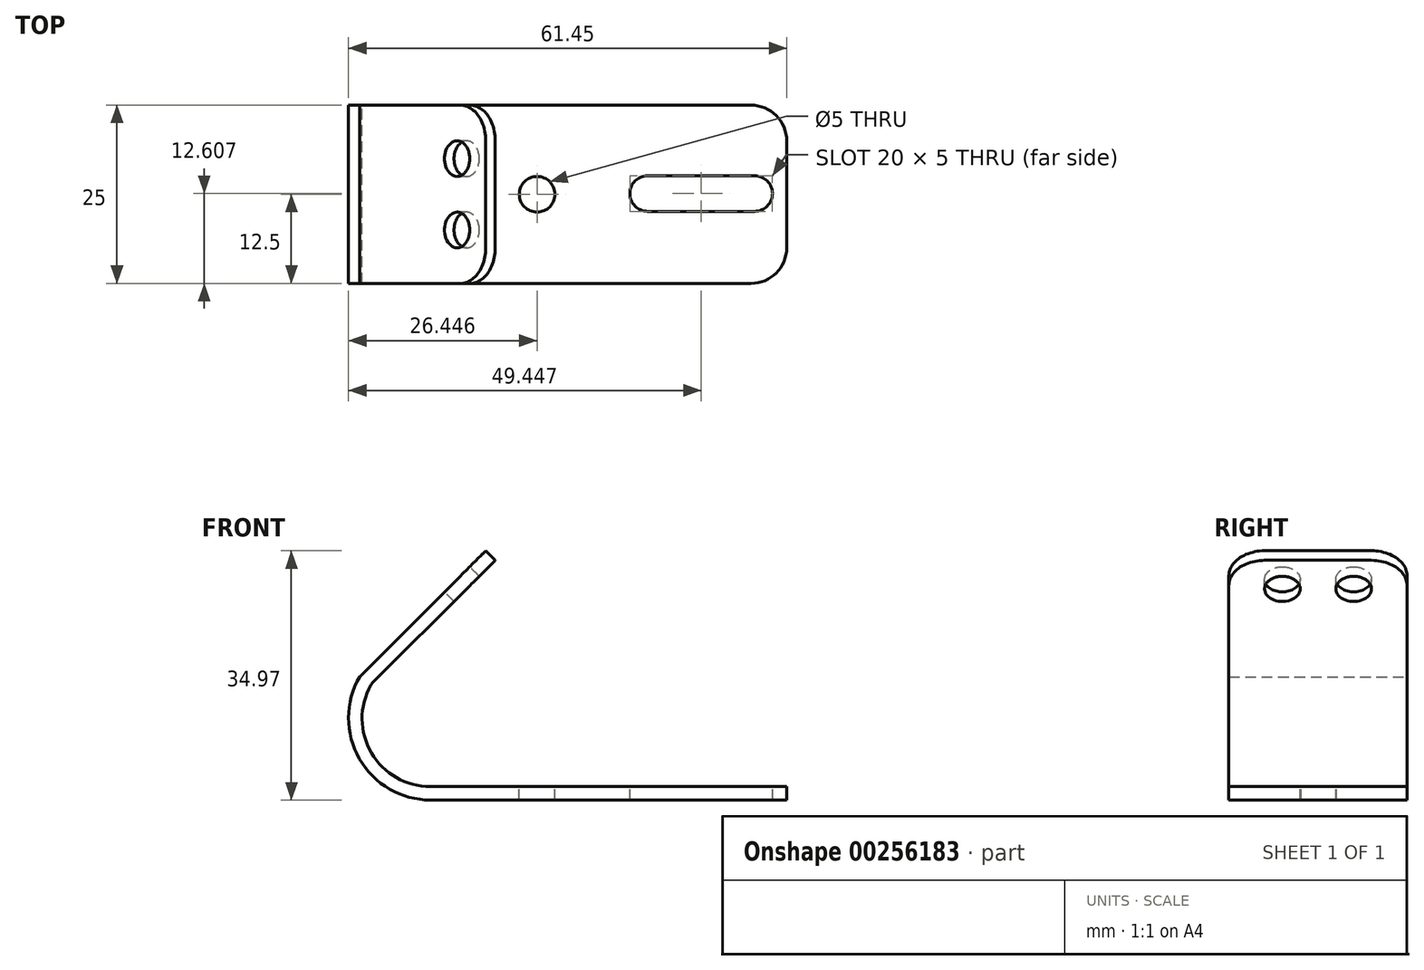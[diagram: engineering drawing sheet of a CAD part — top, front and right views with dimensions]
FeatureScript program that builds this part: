
annotation { "Feature Type Name" : "Feature", "Feature Type Description" : "" }
export const myFeature = defineFeature(function(context is Context, id is Id, definition is map)
    precondition{}
    {
        {
            var Q0;
            Q0=qCreatedBy(makeId("Front.planeOp"),FACE);
            var sketch = newSketch(context, id + "F0", { "sketchPlane" : qUnion([Q0])});
            skLineSegment(sketch, "E0", {"start": v(39.72, 0) * mm, "end": v(-10.22, 0) * mm});
            skLineSegment(sketch, "E1", {"start": v(39.72, 0) * mm, "end": v(39.72, 1.9) * mm});
            skLineSegment(sketch, "E2", {"start": v(39.72, 1.9) * mm, "end": v(-10.28, 1.9) * mm});
            skLineSegment(sketch, "E3", {"start": v(-18.53, 16.25) * mm, "end": v(-1.15, 33.63) * mm});
            skLineSegment(sketch, "E4", {"start": v(-1.15, 33.63) * mm, "end": v(-2.5, 34.97) * mm});
            skLineSegment(sketch, "E5", {"start": v(-2.5, 34.97) * mm, "end": v(-20.17, 17.3) * mm});
            skArc(sketch, "E6", {"start": v(-10.22, 0) * mm, "mid": v(-20.2, 5.77) * mm, "end": v(-20.17, 17.3) * mm});
            skArc(sketch, "E7", {"start": v(-10.28, 1.9) * mm, "mid": v(-18.56, 6.69) * mm, "end": v(-18.53, 16.25) * mm});
            skSolve(sketch);
        }
        {
            var Q0;
            Q0=makeQuery(id+"F0.imprint","IMPRINT",FACE,{"disambiguationData":[TD([[makeQuery(id+"F0.imprint","IMPRINT",EDGE,{"derivedFrom":sQuery(id+"F0.wireOp",EDGE,"E0")}),-1.0]])]});
            extrude(context, id + "F1", {"entities" : qUnion([Q0]), "endBound" : BoundingType.SYMMETRIC, "depth" : 25 * mm});
        }
        {
            var Q0;
            Q0=makeQuery(id+"F1.opExtrude","SWEPT_FACE",FACE,{"disambiguationData":[OSD([sQuery(id+"F0.wireOp",EDGE,"E2")])]});
            var sketch = newSketch(context, id + "F2", { "sketchPlane" : qUnion([Q0])});
            skPoint(sketch, "E8", {"position": v(0, 0) * mm});
            skCircle(sketch, "E9", {"center": v(4.72, 0) * mm, "radius": 2.5 * mm});
            skLineSegment(sketch, "E10", {"start": v(20.22, 2.6) * mm, "end": v(35.22, 2.6) * mm});
            skLineSegment(sketch, "E11", {"start": v(35.22, -2.4) * mm, "end": v(20.22, -2.4) * mm});
            skArc(sketch, "E12", {"start": v(35.22, 2.6) * mm, "mid": v(37.72, 0.1) * mm, "end": v(35.22, -2.4) * mm});
            skArc(sketch, "E13", {"start": v(20.22, -2.4) * mm, "mid": v(17.72, 0.1) * mm, "end": v(20.22, 2.6) * mm});
            skSolve(sketch);
        }
        {
            var Q0;
            Q0=makeQuery(id+"F2.imprint","IMPRINT",FACE,{"disambiguationData":[TD([[makeQuery(id+"F2.imprint","IMPRINT",EDGE,{"derivedFrom":sQuery(id+"F2.wireOp",EDGE,"E9")}),1.0]])]});
            var Q1;
            Q1=makeQuery(id+"F2.imprint","IMPRINT",FACE,{"disambiguationData":[TD([[makeQuery(id+"F2.imprint","IMPRINT",EDGE,{"derivedFrom":sQuery(id+"F2.wireOp",EDGE,"E10")}),-1.0]])]});
            extrude(context, id + "F3", {"entities" : qUnion([Q0, Q1]), "operationType" : NewBodyOperationType.REMOVE, "oppositeDirection" : true, "depth" : 25 * mm});
        }
        {
            var Q0;
            Q0=makeQuery(id+"F1.opExtrude","SWEPT_FACE",FACE,{"disambiguationData":[OSD([sQuery(id+"F0.wireOp",EDGE,"E5")])]});
            var sketch = newSketch(context, id + "F4", { "sketchPlane" : qUnion([Q0])});
            skPoint(sketch, "E14", {"position": v(-5, 17.3) * mm});
            skPoint(sketch, "E15", {"position": v(5, 17.3) * mm});
            skSolve(sketch);
        }
        {
            var Q0;
            Q0=sQuery(id+"F4.wireOp",VERTEX,"E14");
            var Q1;
            Q1=sQuery(id+"F4.wireOp",VERTEX,"E15");
            var Q2;
            Q2=makeQuery(id+"F1.opExtrude","SWEPT_BODY",BODY,{"disambiguationData":[OSD([sQuery(id+"F0.wireOp",EDGE,"E0"),sQuery(id+"F0.wireOp",EDGE,"E1"),sQuery(id+"F0.wireOp",EDGE,"E2"),sQuery(id+"F0.wireOp",EDGE,"E3"),sQuery(id+"F0.wireOp",EDGE,"E4"),sQuery(id+"F0.wireOp",EDGE,"E5"),sQuery(id+"F0.wireOp",EDGE,"E6"),sQuery(id+"F0.wireOp",EDGE,"E7")])]});
            hole(context, id + "F5", {"style" : HoleStyle.C_BORE, "endStyle" : HoleEndStyle.BLIND, "holeDiameter" : 5 * mm, "cBoreDiameter" : 5 * mm, "cBoreDepth" : 5 * mm, "holeDepth" : 12 * mm, "tappedDepth" : 12 * mm, "tapClearance" : 3, "locations" : qUnion([Q0, Q1]), "scope" : qUnion([Q2])});
        }
        {
            var Q0;
            Q0=makeQuery(id+"F1.opExtrude","CAP_EDGE",EDGE,{"disambiguationData":[OSD([sQuery(id+"F0.wireOp",EDGE,"E1")])],"isStart":false});
            var Q1;
            Q1=makeQuery(id+"F1.opExtrude","CAP_EDGE",EDGE,{"disambiguationData":[OSD([sQuery(id+"F0.wireOp",EDGE,"E1")])],"isStart":true});
            fillet(context, id + "F6", {"entities" : qUnion([Q0, Q1]), "radius" : 5 * mm, "tangentPropagation" : true, "allowEdgeOverflow" : false});
        }
        {
            var Q0;
            Q0=makeQuery(id+"F1.opExtrude","CAP_EDGE",EDGE,{"disambiguationData":[OSD([sQuery(id+"F0.wireOp",EDGE,"E4")])],"isStart":false});
            var Q1;
            Q1=makeQuery(id+"F1.opExtrude","CAP_EDGE",EDGE,{"disambiguationData":[OSD([sQuery(id+"F0.wireOp",EDGE,"E4")])],"isStart":true});
            fillet(context, id + "F7", {"entities" : qUnion([Q0, Q1]), "radius" : 5 * mm, "tangentPropagation" : true, "allowEdgeOverflow" : false});
        }
        {
            var Q0;
            Q0=makeQuery(id+"F1.opExtrude","SWEPT_EDGE",EDGE,{"disambiguationData":[OSD([sQuery(id+"F0.wireOp",EDGE,"E3"),sQuery(id+"F0.wireOp",EDGE,"E7")])]});
            var Q1;
            Q1=makeQuery(id+"F1.opExtrude","SWEPT_EDGE",EDGE,{"disambiguationData":[OSD([sQuery(id+"F0.wireOp",EDGE,"E2"),sQuery(id+"F0.wireOp",EDGE,"E7")])]});
            fillet(context, id + "F8", {"entities" : qUnion([Q0, Q1]), "radius" : 1.2 * mm, "tangentPropagation" : true, "allowEdgeOverflow" : false});
        }
    });
